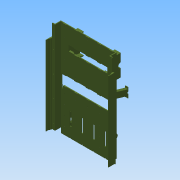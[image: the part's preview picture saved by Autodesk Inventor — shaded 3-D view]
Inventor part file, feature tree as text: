
AUTODESK INVENTOR PART (.ipt)
format: ipt  version: 2015 (Build 190159000, 159)  size: 1,020,416 bytes
history: native  units: mm
features: sketch x49, extrude x47, thread x14, pattern_linear x11, fillet x5, plane x1, loft x1
ambient origin geometry x8: Origin, YZ Plane, XZ Plane, XY Plane, X Axis, Y Axis, Z Axis, Center Point
bodies: 实体1 (feature_tree)
feature tree (128):
  extrude  "拉伸1"  Depth=8.0mm
  extrude  "拉伸2"  Depth=52.5mm
  extrude  "拉伸3"  Depth=5.0mm
  extrude  "拉伸4"  Depth=12.5mm
  pattern_linear  "矩形阵列1"  Count1=3  [1 undecoded]
  extrude  "拉伸5"  Depth=8.0mm
  extrude  "拉伸6"  Depth=60.0mm
  extrude  "拉伸7"  Depth=8.0mm
  extrude  "拉伸8"  Depth=132.5mm
  pattern_linear  "矩形阵列2"  Count1=5  [1 undecoded]
  extrude  "拉伸9"  Depth=398.0mm
  pattern_linear  "矩形阵列3"  Count1=20  [1 undecoded]
  extrude  "拉伸10"  Depth=50.0mm TaperAngle=0.0deg
  extrude  "拉伸11"  Depth=560.0mm
  thread  "螺纹1"  [1 undecoded]
  pattern_linear  "矩形阵列4"  Count1=5  [1 undecoded]
  extrude  "拉伸12"  Depth=15.0mm
  thread  "螺纹2"  [1 undecoded]
  pattern_linear  "矩形阵列5"  Count1=4  [1 undecoded]
  pattern_linear  "矩形阵列6"  Count1=2  [1 undecoded]
  extrude  "拉伸13"  Depth=30.0mm
  fillet  "圆角1"  Radius=25.0mm
  extrude  "拉伸14"  Depth=950.0mm TaperAngle=0.0deg
  extrude  "拉伸15"  Depth=13.0mm TaperAngle=0.0deg
  plane  "工作平面1"
  extrude  "拉伸16"  Depth=25.0mm
  pattern_linear  "矩形阵列7"  Count1=2  [1 undecoded]
  extrude  "拉伸17"  Depth=10.0mm TaperAngle=0.0deg
  extrude  "拉伸18"  Depth=5.0mm
  extrude  "拉伸19"  Depth=20.0mm
  extrude  "拉伸20"  Depth=10.0mm TaperAngle=0.0deg
  fillet  "圆角2"  Radius=40.0mm
  extrude  "拉伸21"  Depth=483.0mm
  pattern_linear  "矩形阵列8"  Count1=4  [1 undecoded]
  extrude  "拉伸22"  Depth=690.0mm
  pattern_linear  "矩形阵列9"  Spacing1=81.0mm  [1 undecoded]
  extrude  "拉伸23"  Depth=81.0mm
  extrude  "拉伸24"  Depth=81.0mm
  extrude  "拉伸25"  Depth=60.0mm
  extrude  "拉伸26"  Depth=60.0mm
  extrude  "拉伸27"  Depth=60.0mm
  extrude  "拉伸28"  Depth=22.0mm TaperAngle=0.0deg
  extrude  "拉伸29"  [1 undecoded]
  extrude  "拉伸30"  Depth=57.0mm
  extrude  "拉伸31"  Depth=175.379mm
  thread  "螺纹3"  [1 undecoded]
  thread  "螺纹4"  [1 undecoded]
  thread  "螺纹5"  [1 undecoded]
  thread  "螺纹6"  [1 undecoded]
  extrude  "拉伸32"  Depth=10.5mm
  pattern_linear  "矩形阵列10"  Count1=3 Spacing1=0.0mm
  extrude  "拉伸33"  Depth=20.0mm
  thread  "螺纹7"  [1 undecoded]
  thread  "螺纹8"  [1 undecoded]
  thread  "螺纹9"  [1 undecoded]
  thread  "螺纹10"  [1 undecoded]
  extrude  "拉伸34"  Depth=37.0mm
  loft  "放样1"
  extrude  "拉伸35"  Depth=28.0mm
  thread  "螺纹11"  [1 undecoded]
  thread  "螺纹12"  [1 undecoded]
  thread  "螺纹13"  [1 undecoded]
  thread  "螺纹14"  [1 undecoded]
  pattern_linear  "矩形阵列11"  Spacing1=5.0mm  [1 undecoded]
  extrude  "拉伸36"  Depth=5.0mm
  fillet  "圆角3"  Radius=7.0mm
  extrude  "拉伸37"  Depth=7.0mm
  extrude  "拉伸38"  Depth=7.0mm
  fillet  "圆角4"  Radius=7.0mm
  extrude  "拉伸39"  Depth=7.0mm
  extrude  "拉伸40"  Depth=7.0mm
  extrude  "拉伸42"  Depth=7.0mm
  extrude  "拉伸43"  Depth=7.0mm
  extrude  "拉伸44"  Depth=5.0mm TaperAngle=0.0deg
  extrude  "拉伸45"  Depth=20.0mm
  fillet  "圆角6"  Radius=50.0mm
  extrude  "拉伸46"  TaperAngle=60.0deg  [1 undecoded]
  extrude  "拉伸47"  Depth=39.5mm
  extrude  "拉伸48"  Depth=10.0mm
  sketch  "草图1"  dims[d0=650.0mm d1=8.0mm]
  sketch  "草图2"  dims[d2=5.0mm d3=52.5mm]
  sketch  "草图3"  dims[d4=12.5mm d5=5.0mm]
  sketch  "草图4"  dims[d8=5.0mm d9=12.5mm]
  sketch  "草图5"  dims[d10=5.0mm]
  sketch  "草图6"  dims[d11=10.0mm]
  sketch  "草图7"  dims[d12=5.0mm]
  sketch  "草图8"  dims[d14=45.0deg]
  sketch  "草图9"  dims[d15=10.0mm]
  sketch  "草图10"  dims[d16=5.0mm]
  sketch  "草图11"  dims[d17=135.0deg]
  sketch  "草图12"  dims[d18=10.0mm]
  sketch  "草图13"  dims[d19=8.0mm d20=30.0mm]
  sketch  "草图14"  dims[d21=60.0mm d22=8.0mm]
  sketch  "草图15"  dims[d23=30.0mm d24=60.0mm]
  sketch  "草图16"  dims[d25=8.0mm d26=8.0mm]
  sketch  "草图17"  dims[d27=900.0mm d28=0.0mm d29=132.5mm]
  sketch  "草图18"  dims[d30=15.0mm d31=0.0mm]
  sketch  "草图19"  dims[d32=132.5mm]
  sketch  "草图20"  dims[d33=15.0mm d34=0.0mm]
  sketch  "草图21"  dims[d35=8.0mm]
  sketch  "草图22"  dims[d36=26.0mm]
  sketch  "草图23"  dims[d37=10.0mm]
  sketch  "草图24"  dims[d38=8.0mm]
  sketch  "草图25"  dims[d39=26.0mm]
  sketch  "草图26"  dims[d40=10.0mm]
  sketch  "草图27"  dims[d41=8.0mm d42=0.0mm d43=50.0mm d45=220.0mm]
  sketch  "草图28"  dims[d46=50.0mm d47=0.0mm d48=398.0mm]
  sketch  "草图29"  dims[d49=56.0mm d50=200.0mm]
  sketch  "草图30"  dims[d51=325.0mm d52=50.0mm d53=0.0mm]
  sketch  "草图31"  dims[d54=460.0mm d55=560.0mm d56=15.0mm d57=50.0mm]
  sketch  "草图32"  dims[d58=8.0mm d59=0.0mm d60=15.0mm d61=755.0mm]
  sketch  "草图33"  dims[d62=892.0mm]
  sketch  "草图34"  dims[d63=100.5mm]
  sketch  "草图35"  dims[d64=8.0mm d65=0.0mm d66=40.0mm d68=120.0mm d69=20.0mm]
  sketch  "草图36"  dims[d70=40.0mm d71=30.0mm d72=25.0mm]
  sketch  "草图37"  dims[d73=5.0mm d74=950.0mm d75=0.0mm]
  sketch  "草图38"  dims[d76=50.0mm d78=120.0mm d79=13.0mm d80=0.0mm]
  sketch  "草图39"  dims[d81=5.0mm d82=25.0mm d83=20.0mm]
  sketch  "草图40"  dims[d84=13.0mm d85=0.0mm d86=10.0mm d87=0.0mm]
  sketch  "草图41"  dims[d88=50.0mm d90=100.0mm d91=5.0mm]
  sketch  "草图42"  dims[d92=25.0mm d93=20.0mm]
  sketch  "草图44"  dims[d94=13.0mm d95=0.0mm d96=10.0mm d97=0.0mm d98=40.0mm d100=100.0mm]
  sketch  "草图45"  dims[d101=50.0mm d103=120.0mm d104=483.0mm d105=40.0mm]
  sketch  "草图46"  dims[d106=20.0mm d107=690.0mm]
  sketch  "草图47"  dims[d108=22.0mm d109=0.0mm]
  sketch  "草图48"  dims[d110=10.0mm]
  sketch  "草图49"  dims[d111=10.0mm]
  sketch  "草图50"  dims[d112=22.0mm d113=0.0mm d114=81.0mm d115=81.0mm d116=81.0mm d117=60.0mm d118=60.0mm d119=60.0mm d120=22.0mm d121=0.0mm d122=-40.0mm d123=57.0mm d124=175.379mm d125=450.0mm d126=472.654mm d127=100.0mm d128=5.0mm d129=10.5mm d130=30.0mm d131=0.0mm d132=20.0mm d134=453.0mm d135=37.0mm d136=9.0mm d137=0.0mm d138=28.0mm d139=5.0mm d140=0.0mm d141=37.0mm d142=9.0mm d143=0.0mm d144=28.0mm d145=5.0mm d146=0.0mm d147=4.0mm d148=5.0mm d149=5.0mm d150=5.0mm d151=5.0mm d152=7.0mm d153=7.0mm d154=7.0mm d155=7.0mm d156=7.0mm d157=7.0mm d158=7.0mm d159=7.0mm d160=5.0mm d161=0.0mm d162=20.0mm d164=453.0mm d165=50.0mm d166=60.0deg d167=39.5mm d168=800.0mm d169=18.0mm d170=0.0mm d171=20.0mm d173=465.0mm d174=50.0mm d175=5.0mm d176=0.0mm d177=32.0mm d178=13.0mm d179=0.0mm d180=32.0mm d181=9.0mm d182=0.0mm d183=24.0mm d184=3.0mm d185=0.0mm d186=15.0mm d187=3.0mm d188=0.0mm d189=4.0mm d190=4.0mm d191=4.0mm d192=4.0mm d193=10.0mm d194=10.0mm d195=10.0mm d196=10.0mm d197=20.5mm d198=10.0mm d199=10.0mm d200=13.0mm d201=0.0mm d202=23.0mm d203=90.0mm d204=66.0mm d205=220.0mm d206=23.0mm d207=90.0mm d208=66.0mm d209=220.0mm d210=109.5mm d211=0.0mm d212=52.0mm d213=109.5mm d214=0.0mm d215=5.0mm d216=5.0mm d217=36.25mm d218=45.0deg d219=109.5mm d220=0.0mm d221=10.0mm d222=0.0mm d223=10.0mm d224=0.0mm d225=10.0mm d226=0.0mm d227=10.0mm d228=0.0mm d229=206.0mm d230=56.0mm d231=103.0mm d232=103.0mm d233=38.0mm d234=0.0mm d235=20.0mm d237=360.0mm d238=8.0mm d239=8.0mm d240=8.0mm d241=8.0mm d242=110.0mm d243=55.0mm d244=11.5mm d245=11.5mm d246=110.0mm d247=55.0mm d248=11.5mm d249=11.5mm d250=22.0mm d251=0.0mm d252=10.0mm d253=0.0mm d254=10.0mm d255=0.0mm d256=10.0mm d257=0.0mm d258=10.0mm d259=0.0mm d260=50.0mm d261=0.0mm d262=10.0mm d263=20.0mm d264=7.5mm d265=28.0mm d266=7.5mm d267=0.0mm d268=90.0deg d269=0.0mm d270=90.0deg d272=3.0mm d273=3.0mm d274=3.0mm d276=20.0mm d277=2.5mm d278=3.0mm d279=2.5mm d280=2.5mm d281=2.5mm d282=3.0mm d283=3.0mm d284=3.0mm d285=3.0mm d286=50.0mm d287=0.0mm d288=10.0mm d289=0.0mm d290=10.0mm d291=0.0mm d292=10.0mm d293=0.0mm d294=10.0mm d295=0.0mm d296=40.0mm d298=120.0mm d299=130.0mm d300=65.0mm d301=104.5mm d302=10.0mm d303=10.0mm d304=10.0mm d305=10.0mm d306=18.0mm d307=0.0mm d308=5.0mm d309=25.0mm d310=3.0mm d311=20.0mm d312=50.0mm d313=114.5mm d314=0.0mm d315=32.0mm d316=50.0mm d317=20.0mm d318=0.0mm d319=25.0mm d320=37.0mm d321=40.0mm d322=400.0mm d323=160.0mm d324=0.0mm d325=10.0mm d326=10.0mm d327=0.0mm d332=15.0mm d333=49.984mm d334=31.848mm d335=31.27mm d336=0.0mm d337=20.0mm d338=2.0mm d339=0.0mm d340=32.0mm d341=20.507mm d342=74.431mm d343=2.0mm d344=0.0mm d345=32.0mm d346=2.0mm d347=0.0mm d348=5.0mm d349=15.0mm d350=21.101mm d351=23.786mm d352=26.27mm d353=0.0mm d354=20.0mm d355=2.0mm d356=0.0mm d357=26.0mm d358=17.0mm d359=19.0mm d360=10.0mm d361=0.0mm]
note: 26 required parameter values undecoded (feature->parameter linkage not recoverable at this tier; creation-order binding heuristic only, values carry confidence <= 0.55)
